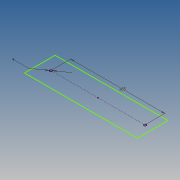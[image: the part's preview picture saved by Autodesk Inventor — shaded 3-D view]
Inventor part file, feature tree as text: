
AUTODESK INVENTOR PART (.ipt)
format: ipt  version: 2017 (Build 210142000, 142)  size: 67,072 bytes
history: native  units: mm
features: sketch x1
ambient origin geometry x8: Origin, YZ Plane, XZ Plane, XY Plane, X Axis, Y Axis, Z Axis, Center Point
feature tree (1):
  sketch  "Boceto1"  dims[d0=165.0mm d1=4.0mm]
